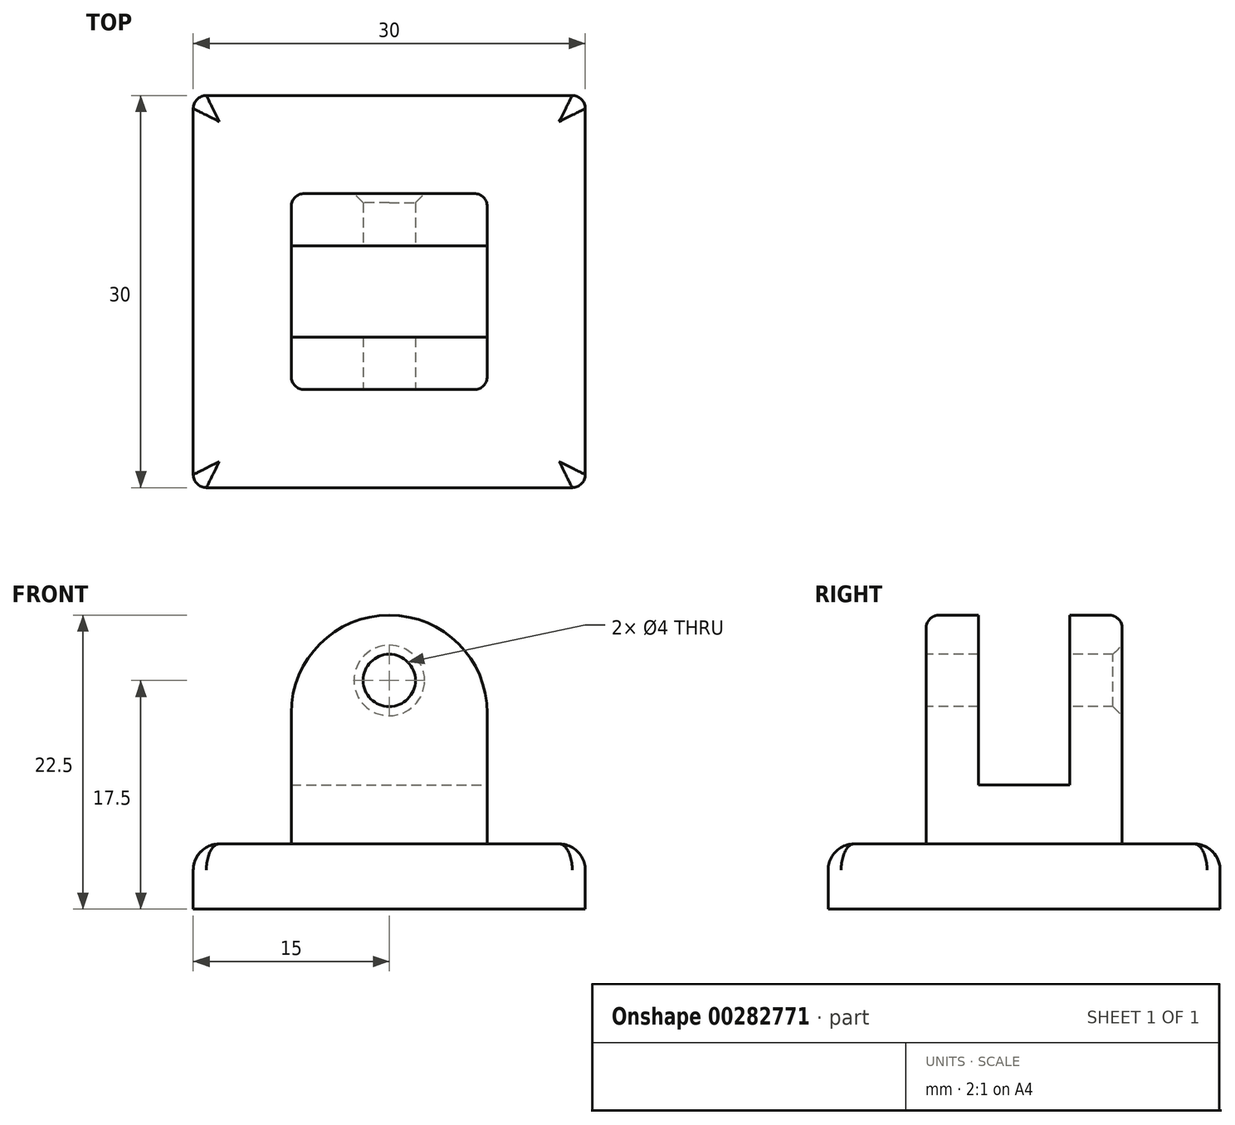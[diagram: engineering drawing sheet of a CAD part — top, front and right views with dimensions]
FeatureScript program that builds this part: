
annotation { "Feature Type Name" : "Feature", "Feature Type Description" : "" }
export const myFeature = defineFeature(function(context is Context, id is Id, definition is map)
    precondition{}
    {
        {
            var Q0;
            Q0=qCreatedBy(makeId("Front.planeOp"),FACE);
            var sketch = newSketch(context, id + "F0", { "sketchPlane" : qUnion([Q0])});
            skLineSegment(sketch, "E0.bottom", {"start": v(0, 0) * mm, "end": v(30, 0) * mm});
            skLineSegment(sketch, "E0.top", {"start": v(0, 5) * mm, "end": v(30, 5) * mm});
            skLineSegment(sketch, "E0.left", {"start": v(0, 0) * mm, "end": v(0, 5) * mm});
            skLineSegment(sketch, "E0.right", {"start": v(30, 0) * mm, "end": v(30, 5) * mm});
            skSolve(sketch);
        }
        {
            var Q0;
            Q0=makeQuery(id+"F0.imprint","IMPRINT",FACE,{"disambiguationData":[TD([[makeQuery(id+"F0.imprint","IMPRINT",EDGE,{"derivedFrom":sQuery(id+"F0.wireOp",EDGE,"E0.bottom")}),1.0]])]});
            extrude(context, id + "F1", {"entities" : qUnion([Q0]), "oppositeDirection" : true, "depth" : 30 * mm});
        }
        {
            var Q0;
            Q0=makeQuery(id+"F1.opExtrude","SWEPT_FACE",FACE,{"disambiguationData":[OSD([sQuery(id+"F0.wireOp",EDGE,"E0.top")])]});
            var sketch = newSketch(context, id + "F2", { "sketchPlane" : qUnion([Q0])});
            skLineSegment(sketch, "E1.bottom", {"start": v(7.5, 22.5) * mm, "end": v(22.5, 22.5) * mm});
            skLineSegment(sketch, "E1.top", {"start": v(7.5, 7.5) * mm, "end": v(22.5, 7.5) * mm});
            skLineSegment(sketch, "E1.left", {"start": v(7.5, 22.5) * mm, "end": v(7.5, 7.5) * mm});
            skLineSegment(sketch, "E1.right", {"start": v(22.5, 22.5) * mm, "end": v(22.5, 7.5) * mm});
            skPoint(sketch, "E1.middle", {"position": v(15, 15) * mm});
            skSolve(sketch);
        }
        {
            var Q0;
            Q0 = qSketchRegion(id + "F2", true);
            extrude(context, id + "F3", {"entities" : qUnion([Q0]), "operationType" : NewBodyOperationType.ADD, "depth" : 17.5 * mm});
        }
        {
            var Q0;
            Q0=makeQuery(id+"F3.opExtrude","CAP_FACE",FACE,{"disambiguationData":[OSD([sQuery(id+"F2.wireOp",EDGE,"E1.bottom"),sQuery(id+"F2.wireOp",EDGE,"E1.top"),sQuery(id+"F2.wireOp",EDGE,"E1.left"),sQuery(id+"F2.wireOp",EDGE,"E1.right")])],"isStart":false});
            var sketch = newSketch(context, id + "F4", { "sketchPlane" : qUnion([Q0])});
            skLineSegment(sketch, "E2.bottom", {"start": v(-2.47, 11.5) * mm, "end": v(34.32, 11.5) * mm});
            skLineSegment(sketch, "E2.top", {"start": v(-2.47, 18.5) * mm, "end": v(34.32, 18.5) * mm});
            skLineSegment(sketch, "E2.left", {"start": v(-2.47, 11.5) * mm, "end": v(-2.47, 18.5) * mm});
            skLineSegment(sketch, "E2.right", {"start": v(34.32, 11.5) * mm, "end": v(34.32, 18.5) * mm});
            skSolve(sketch);
        }
        {
            var Q0;
            Q0 = qSketchRegion(id + "F4", true);
            extrude(context, id + "F5", {"entities" : qUnion([Q0]), "operationType" : NewBodyOperationType.REMOVE, "oppositeDirection" : true, "depth" : 13 * mm});
        }
        {
            var Q0;
            Q0=makeQuery(id+"F3.opExtrude","SWEPT_FACE",FACE,{"disambiguationData":[OSD([sQuery(id+"F2.wireOp",EDGE,"E1.top")])]});
            var sketch = newSketch(context, id + "F6", { "sketchPlane" : qUnion([Q0])});
            skCircle(sketch, "E3", {"center": v(15, 17.5) * mm, "radius": 2 * mm});
            skSolve(sketch);
        }
        {
            var Q0;
            Q0 = qSketchRegion(id + "F6", true);
            extrude(context, id + "F7", {"entities" : qUnion([Q0]), "operationType" : NewBodyOperationType.REMOVE, "oppositeDirection" : true, "depth" : 25 * mm});
        }
        {
            var Q0;
            {var subQ0=sQuery(id+"F2.wireOp",EDGE,"E1.left");var subQ1=sQuery(id+"F2.wireOp",EDGE,"E1.top");Q0=makeQuery(id+"F5.boolean.opBoolean","SPLIT",EDGE,{"disambiguationData":[TD([makeQuery(id+"F3.opExtrude","SWEPT_FACE",FACE,{"disambiguationData":[OSD([subQ1])]})])],"derivedFrom":makeQuery(id+"F3.opExtrude","CAP_EDGE",EDGE,{"disambiguationData":[OSD([subQ0])],"isStart":false})});}
            fillet(context, id + "F8", {"entities" : qUnion([Q0]), "radius" : 7.5 * mm, "tangentPropagation" : true, "allowEdgeOverflow" : false});
        }
        {
            var Q0;
            {var subQ0=sQuery(id+"F2.wireOp",EDGE,"E1.bottom");var subQ1=sQuery(id+"F2.wireOp",EDGE,"E1.left");Q0=makeQuery(id+"F5.boolean.opBoolean","SPLIT",EDGE,{"disambiguationData":[TD([makeQuery(id+"F3.opExtrude","SWEPT_FACE",FACE,{"disambiguationData":[OSD([subQ0])]})])],"derivedFrom":makeQuery(id+"F3.opExtrude","CAP_EDGE",EDGE,{"disambiguationData":[OSD([subQ1])],"isStart":false})});}
            var Q1;
            {var subQ0=sQuery(id+"F2.wireOp",EDGE,"E1.bottom");var subQ1=sQuery(id+"F2.wireOp",EDGE,"E1.right");Q1=makeQuery(id+"F5.boolean.opBoolean","SPLIT",EDGE,{"disambiguationData":[TD([makeQuery(id+"F3.opExtrude","SWEPT_FACE",FACE,{"disambiguationData":[OSD([subQ0])]})])],"derivedFrom":makeQuery(id+"F3.opExtrude","CAP_EDGE",EDGE,{"disambiguationData":[OSD([subQ1])],"isStart":false})});}
            var Q2;
            {var subQ0=sQuery(id+"F2.wireOp",EDGE,"E1.right");var subQ1=sQuery(id+"F2.wireOp",EDGE,"E1.top");Q2=makeQuery(id+"F5.boolean.opBoolean","SPLIT",EDGE,{"disambiguationData":[TD([makeQuery(id+"F3.opExtrude","SWEPT_FACE",FACE,{"disambiguationData":[OSD([subQ1])]})])],"derivedFrom":makeQuery(id+"F3.opExtrude","CAP_EDGE",EDGE,{"disambiguationData":[OSD([subQ0])],"isStart":false})});}
            fillet(context, id + "F9", {"entities" : qUnion([Q0, Q1, Q2]), "radius" : 7.5 * mm, "tangentPropagation" : true, "allowEdgeOverflow" : false});
        }
        {
            var Q0;
            Q0=makeQuery(id+"F1.opExtrude","SWEPT_EDGE",EDGE,{"disambiguationData":[OSD([sQuery(id+"F0.wireOp",EDGE,"E0.top"),sQuery(id+"F0.wireOp",EDGE,"E0.left")])]});
            var Q1;
            Q1=makeQuery(id+"F1.opExtrude","CAP_EDGE",EDGE,{"disambiguationData":[OSD([sQuery(id+"F0.wireOp",EDGE,"E0.top")])],"isStart":true});
            var Q2;
            Q2=makeQuery(id+"F1.opExtrude","SWEPT_EDGE",EDGE,{"disambiguationData":[OSD([sQuery(id+"F0.wireOp",EDGE,"E0.top"),sQuery(id+"F0.wireOp",EDGE,"E0.right")])]});
            var Q3;
            Q3=makeQuery(id+"F1.opExtrude","CAP_EDGE",EDGE,{"disambiguationData":[OSD([sQuery(id+"F0.wireOp",EDGE,"E0.top")])],"isStart":false});
            fillet(context, id + "F10", {"entities" : qUnion([Q0, Q1, Q2, Q3]), "radius" : 2 * mm, "tangentPropagation" : true, "allowEdgeOverflow" : false});
        }
        {
            var Q0;
            Q0=makeQuery(id+"F3.opExtrude","SWEPT_EDGE",EDGE,{"disambiguationData":[OSD([sQuery(id+"F2.wireOp",EDGE,"E1.top"),sQuery(id+"F2.wireOp",EDGE,"E1.left")])]});
            var Q1;
            Q1=makeQuery(id+"F3.opExtrude","SWEPT_EDGE",EDGE,{"disambiguationData":[OSD([sQuery(id+"F2.wireOp",EDGE,"E1.bottom"),sQuery(id+"F2.wireOp",EDGE,"E1.right")])]});
            var Q2;
            Q2=makeQuery(id+"F1.opExtrude","CAP_EDGE",EDGE,{"disambiguationData":[OSD([sQuery(id+"F0.wireOp",EDGE,"E0.right")])],"isStart":true});
            var Q3;
            Q3=makeQuery(id+"F1.opExtrude","CAP_EDGE",EDGE,{"disambiguationData":[OSD([sQuery(id+"F0.wireOp",EDGE,"E0.left")])],"isStart":true});
            var Q4;
            Q4=makeQuery(id+"F1.opExtrude","CAP_EDGE",EDGE,{"disambiguationData":[OSD([sQuery(id+"F0.wireOp",EDGE,"E0.right")])],"isStart":false});
            var Q5;
            {var subQ0=sQuery(id+"F2.wireOp",EDGE,"E1.top");var subQ1=makeQuery(id+"F3.opExtrude","SWEPT_FACE",FACE,{"disambiguationData":[OSD([subQ0])]});var subQ2=sQuery(id+"F2.wireOp",EDGE,"E1.right");Q5=makeQuery(id+"F9.opFillet","BLEND_EDGE",EDGE,{"blendedFrom":[makeQuery(id+"F5.boolean.opBoolean","SPLIT",EDGE,{"disambiguationData":[TD([subQ1])],"derivedFrom":makeQuery(id+"F3.opExtrude","CAP_EDGE",EDGE,{"disambiguationData":[OSD([subQ2])],"isStart":false})}),subQ1],"blendedInto":[subQ1]});}
            var Q6;
            {var subQ0=sQuery(id+"F2.wireOp",EDGE,"E1.top");var subQ1=makeQuery(id+"F3.opExtrude","SWEPT_FACE",FACE,{"disambiguationData":[OSD([subQ0])]});var subQ2=sQuery(id+"F2.wireOp",EDGE,"E1.left");Q6=makeQuery(id+"F8.opFillet","BLEND_EDGE",EDGE,{"blendedFrom":[makeQuery(id+"F5.boolean.opBoolean","SPLIT",EDGE,{"disambiguationData":[TD([subQ1])],"derivedFrom":makeQuery(id+"F3.opExtrude","CAP_EDGE",EDGE,{"disambiguationData":[OSD([subQ2])],"isStart":false})}),subQ1],"blendedInto":[subQ1]});}
            var Q7;
            {var subQ0=sQuery(id+"F2.wireOp",EDGE,"E1.bottom");var subQ1=makeQuery(id+"F3.opExtrude","SWEPT_FACE",FACE,{"disambiguationData":[OSD([subQ0])]});var subQ2=sQuery(id+"F2.wireOp",EDGE,"E1.left");Q7=makeQuery(id+"F9.opFillet","BLEND_EDGE",EDGE,{"blendedFrom":[makeQuery(id+"F5.boolean.opBoolean","SPLIT",EDGE,{"disambiguationData":[TD([subQ1])],"derivedFrom":makeQuery(id+"F3.opExtrude","CAP_EDGE",EDGE,{"disambiguationData":[OSD([subQ2])],"isStart":false})}),subQ1],"blendedInto":[subQ1]});}
            fillet(context, id + "F11", {"entities" : qUnion([Q0, Q1, Q2, Q3, Q4, Q5, Q6, Q7]), "radius" : 1 * mm, "tangentPropagation" : true, "allowEdgeOverflow" : false});
        }
        {
            var Q0;
            Q0=makeQuery(id+"F1.opExtrude","CAP_EDGE",EDGE,{"disambiguationData":[OSD([sQuery(id+"F0.wireOp",EDGE,"E0.left")])],"isStart":false});
            fillet(context, id + "F12", {"entities" : qUnion([Q0]), "radius" : 1 * mm, "tangentPropagation" : true, "allowEdgeOverflow" : false});
        }
        {
            var Q0;
            Q0=makeQuery(id+"F7.boolean.opBoolean","COPY",EDGE,{"derivedFrom":makeQuery(id+"F7.opExtrude","CAP_EDGE",EDGE,{"disambiguationData":[OSD([sQuery(id+"F6.wireOp",EDGE,"E3")])],"isStart":true})});
            var Q1;
            Q1=makeQuery(id+"F7.boolean.opBoolean","INTERSECT",EDGE,{"derivedFrom":[makeQuery(id+"F3.opExtrude","SWEPT_FACE",FACE,{"disambiguationData":[OSD([sQuery(id+"F2.wireOp",EDGE,"E1.bottom")])]}),makeQuery(id+"F7.opExtrude","SWEPT_FACE",FACE,{"disambiguationData":[OSD([sQuery(id+"F6.wireOp",EDGE,"E3")])]})]});
            chamfer(context, id + "F13", {"entities" : qUnion([Q0, Q1]), "width" : 0.7 * mm, "tangentPropagation" : true});
        }
    });
